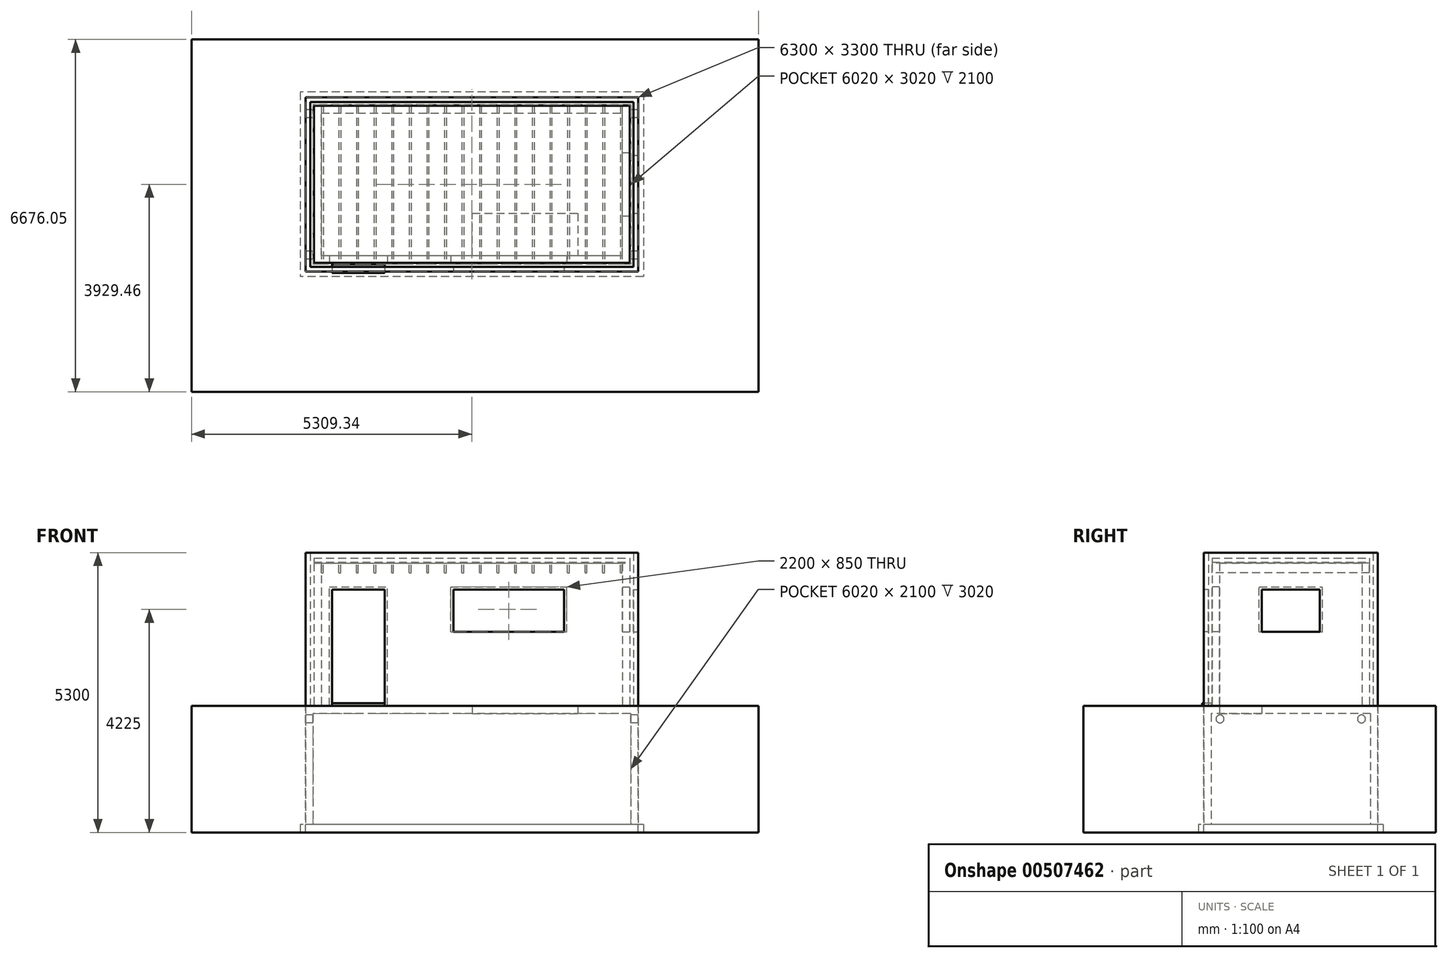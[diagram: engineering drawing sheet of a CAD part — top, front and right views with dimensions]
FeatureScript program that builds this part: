
annotation { "Feature Type Name" : "Feature", "Feature Type Description" : "" }
export const myFeature = defineFeature(function(context is Context, id is Id, definition is map)
    precondition{}
    {
        {
            var Q0;
            Q0=qCreatedBy(makeId("Top.planeOp"),FACE);
            var sketch = newSketch(context, id + "F0", { "sketchPlane" : qUnion([Q0])});
            skLineSegment(sketch, "E0.bottom", {"start": v(3250, 1750) * mm, "end": v(-3250, 1750) * mm});
            skLineSegment(sketch, "E0.top", {"start": v(3250, -1750) * mm, "end": v(-3250, -1750) * mm});
            skLineSegment(sketch, "E0.left", {"start": v(3250, 1750) * mm, "end": v(3250, -1750) * mm});
            skLineSegment(sketch, "E0.right", {"start": v(-3250, 1750) * mm, "end": v(-3250, -1750) * mm});
            skPoint(sketch, "E0.middle", {"position": v(0, 0) * mm});
            skSolve(sketch);
        }
        {
            var Q0;
            Q0=qSketchRegion(id+"F0",true);
            extrude(context, id + "F1", {"entities" : qUnion([Q0]), "depth" : 150 * mm});
        }
        {
            var Q0;
            Q0=makeQuery(id+"F1.opExtrude","CAP_FACE",FACE,{"disambiguationData":[OSD([sQuery(id+"F0.wireOp",EDGE,"E0.bottom"),sQuery(id+"F0.wireOp",EDGE,"E0.top"),sQuery(id+"F0.wireOp",EDGE,"E0.left"),sQuery(id+"F0.wireOp",EDGE,"E0.right")])],"isStart":false});
            var sketch = newSketch(context, id + "F2", { "sketchPlane" : qUnion([Q0])});
            skLineSegment(sketch, "E1.bottom", {"start": v(3010, 1510) * mm, "end": v(-3010, 1510) * mm});
            skLineSegment(sketch, "E1.top", {"start": v(3010, -1510) * mm, "end": v(-3010, -1510) * mm});
            skLineSegment(sketch, "E1.left", {"start": v(3010, 1510) * mm, "end": v(3010, -1510) * mm});
            skLineSegment(sketch, "E1.right", {"start": v(-3010, 1510) * mm, "end": v(-3010, -1510) * mm});
            skPoint(sketch, "E1.middle", {"position": v(0, 0) * mm});
            skLineSegment(sketch, "E2.bottom", {"start": v(3150, 1650) * mm, "end": v(-3150, 1650) * mm});
            skLineSegment(sketch, "E2.top", {"start": v(3150, -1650) * mm, "end": v(-3150, -1650) * mm});
            skLineSegment(sketch, "E2.left", {"start": v(3150, 1650) * mm, "end": v(3150, -1650) * mm});
            skLineSegment(sketch, "E2.right", {"start": v(-3150, 1650) * mm, "end": v(-3150, -1650) * mm});
            skSolve(sketch);
        }
        {
            var Q0;
            Q0=qSketchRegion(id+"F2",true);
            extrude(context, id + "F3", {"entities" : qUnion([Q0]), "operationType" : NewBodyOperationType.ADD, "depth" : 2100 * mm});
        }
        {
            var Q0;
            Q0=makeQuery(id+"F3.opExtrude","CAP_FACE",FACE,{"disambiguationData":[OSD([sQuery(id+"F2.wireOp",EDGE,"E1.bottom"),sQuery(id+"F2.wireOp",EDGE,"E1.top"),sQuery(id+"F2.wireOp",EDGE,"E1.left"),sQuery(id+"F2.wireOp",EDGE,"E1.right"),sQuery(id+"F2.wireOp",EDGE,"E2.bottom"),sQuery(id+"F2.wireOp",EDGE,"E2.top"),sQuery(id+"F2.wireOp",EDGE,"E2.left"),sQuery(id+"F2.wireOp",EDGE,"E2.right")])],"isStart":false});
            var sketch = newSketch(context, id + "F4", { "sketchPlane" : qUnion([Q0])});
            skLineSegment(sketch, "E3", {"start": v(10, -1350) * mm, "end": v(10, -550) * mm});
            skLineSegment(sketch, "E4", {"start": v(10, -550) * mm, "end": v(2010, -550) * mm});
            skLineSegment(sketch, "E5", {"start": v(3150, -1650) * mm, "end": v(3150, 1650) * mm});
            skLineSegment(sketch, "E6", {"start": v(3150, 1650) * mm, "end": v(-3150, 1650) * mm});
            skLineSegment(sketch, "E7", {"start": v(-3150, 1650) * mm, "end": v(-3150, -1650) * mm});
            skLineSegment(sketch, "E8", {"start": v(-3150, -1650) * mm, "end": v(3150, -1650) * mm});
            skLineSegment(sketch, "E9", {"start": v(2010, -550) * mm, "end": v(2010, -1350) * mm});
            skLineSegment(sketch, "E10", {"start": v(10, -1350) * mm, "end": v(2010, -1350) * mm});
            skSolve(sketch);
        }
        {
            var Q0;
            Q0=qSketchRegion(id+"F4",true);
            extrude(context, id + "F5", {"entities" : qUnion([Q0]), "operationType" : NewBodyOperationType.ADD, "depth" : 150 * mm});
        }
        {
            var Q0;
            Q0=makeQuery(id+"F5.boolean.opBoolean","MERGE",FACE,{"derivedFrom":[makeQuery(id+"F3.opExtrude","SWEPT_FACE",FACE,{"disambiguationData":[OSD([sQuery(id+"F2.wireOp",EDGE,"E2.right")])]}),makeQuery(id+"F5.opExtrude","SWEPT_FACE",FACE,{"disambiguationData":[OSD([sQuery(id+"F4.wireOp",EDGE,"E7")])]})]});
            var sketch = newSketch(context, id + "F6", { "sketchPlane" : qUnion([Q0])});
            skCircle(sketch, "E11", {"center": v(-1340, 2150) * mm, "radius": 75 * mm});
            skCircle(sketch, "E12", {"center": v(1340, 2150) * mm, "radius": 75 * mm});
            skSolve(sketch);
        }
        {
            var Q0;
            Q0=qSketchRegion(id+"F6",true);
            extrude(context, id + "F7", {"entities" : qUnion([Q0]), "operationType" : NewBodyOperationType.REMOVE, "endBound" : BoundingType.THROUGH_ALL, "oppositeDirection" : true, "depth" : 25 * mm});
        }
        {
            var Q0;
            Q0=makeQuery(id+"F5.opExtrude","CAP_FACE",FACE,{"disambiguationData":[OSD([sQuery(id+"F4.wireOp",EDGE,"E3"),sQuery(id+"F4.wireOp",EDGE,"E4"),sQuery(id+"F4.wireOp",EDGE,"E5"),sQuery(id+"F4.wireOp",EDGE,"E6"),sQuery(id+"F4.wireOp",EDGE,"E7"),sQuery(id+"F4.wireOp",EDGE,"E8"),sQuery(id+"F4.wireOp",EDGE,"E9"),sQuery(id+"F4.wireOp",EDGE,"E10")])],"isStart":false});
            var sketch = newSketch(context, id + "F8", { "sketchPlane" : qUnion([Q0])});
            skLineSegment(sketch, "E13.bottom", {"start": v(-3150, -1650) * mm, "end": v(3150, -1650) * mm});
            skLineSegment(sketch, "E13.top", {"start": v(-3150, 1650) * mm, "end": v(3150, 1650) * mm});
            skLineSegment(sketch, "E13.left", {"start": v(-3150, -1650) * mm, "end": v(-3150, 1650) * mm});
            skLineSegment(sketch, "E13.right", {"start": v(3150, -1650) * mm, "end": v(3150, 1650) * mm});
            skLineSegment(sketch, "E14.bottom", {"start": v(-3060, -1560) * mm, "end": v(3060, -1560) * mm});
            skLineSegment(sketch, "E14.top", {"start": v(-3060, 1560) * mm, "end": v(3060, 1560) * mm});
            skLineSegment(sketch, "E14.left", {"start": v(-3060, -1560) * mm, "end": v(-3060, 1560) * mm});
            skLineSegment(sketch, "E14.right", {"start": v(3060, -1560) * mm, "end": v(3060, 1560) * mm});
            skSolve(sketch);
        }
        {
            var Q0;
            Q0 = qSketchRegion(id + "F8", true);
            extrude(context, id + "F9", {"entities" : qUnion([Q0]), "depth" : 2900 * mm});
        }
        {
            var Q0;
            Q0=makeQuery(id+"F5.opExtrude","CAP_FACE",FACE,{"disambiguationData":[OSD([sQuery(id+"F4.wireOp",EDGE,"E3"),sQuery(id+"F4.wireOp",EDGE,"E4"),sQuery(id+"F4.wireOp",EDGE,"E5"),sQuery(id+"F4.wireOp",EDGE,"E6"),sQuery(id+"F4.wireOp",EDGE,"E7"),sQuery(id+"F4.wireOp",EDGE,"E8"),sQuery(id+"F4.wireOp",EDGE,"E9"),sQuery(id+"F4.wireOp",EDGE,"E10")])],"isStart":false});
            var sketch = newSketch(context, id + "F10", { "sketchPlane" : qUnion([Q0])});
            skLineSegment(sketch, "E15.bottom", {"start": v(-2990, -1490) * mm, "end": v(2990, -1490) * mm});
            skLineSegment(sketch, "E15.top", {"start": v(-2990, 1490) * mm, "end": v(2990, 1490) * mm});
            skLineSegment(sketch, "E15.left", {"start": v(-2990, -1490) * mm, "end": v(-2990, 1490) * mm});
            skLineSegment(sketch, "E15.right", {"start": v(2990, -1490) * mm, "end": v(2990, 1490) * mm});
            skLineSegment(sketch, "E16.bottom", {"start": v(-2850, -1350) * mm, "end": v(2850, -1350) * mm});
            skLineSegment(sketch, "E16.top", {"start": v(-2850, 1350) * mm, "end": v(2850, 1350) * mm});
            skLineSegment(sketch, "E16.left", {"start": v(-2850, -1350) * mm, "end": v(-2850, 1350) * mm});
            skLineSegment(sketch, "E16.right", {"start": v(2850, -1350) * mm, "end": v(2850, 1350) * mm});
            skSolve(sketch);
        }
        {
            var Q0;
            Q0 = qSketchRegion(id + "F10", true);
            extrude(context, id + "F11", {"entities" : qUnion([Q0]), "depth" : 2700 * mm});
        }
        {
            var Q0;
            Q0=makeQuery(id+"F9.opExtrude","SWEPT_FACE",FACE,{"disambiguationData":[OSD([sQuery(id+"F8.wireOp",EDGE,"E13.bottom")])]});
            var sketch = newSketch(context, id + "F12", { "sketchPlane" : qUnion([Q0])});
            skLineSegment(sketch, "E17.bottom", {"start": v(-2650, 2400) * mm, "end": v(-1650, 2400) * mm});
            skLineSegment(sketch, "E17.top", {"start": v(-2650, 4600) * mm, "end": v(-1650, 4600) * mm});
            skLineSegment(sketch, "E17.left", {"start": v(-2650, 2400) * mm, "end": v(-2650, 4600) * mm});
            skLineSegment(sketch, "E17.right", {"start": v(-1650, 2400) * mm, "end": v(-1650, 4600) * mm});
            skLineSegment(sketch, "E18.bottom", {"start": v(-350, 3800) * mm, "end": v(1750, 3800) * mm});
            skLineSegment(sketch, "E18.top", {"start": v(-350, 4600) * mm, "end": v(1750, 4600) * mm});
            skLineSegment(sketch, "E18.left", {"start": v(-350, 3800) * mm, "end": v(-350, 4600) * mm});
            skLineSegment(sketch, "E18.right", {"start": v(1750, 3800) * mm, "end": v(1750, 4600) * mm});
            skSolve(sketch);
        }
        {
            var Q0;
            Q0 = qSketchRegion(id + "F12", true);
            extrude(context, id + "F13", {"entities" : qUnion([Q0]), "operationType" : NewBodyOperationType.REMOVE, "endBound" : BoundingType.UP_TO_NEXT, "oppositeDirection" : true, "depth" : 25 * mm});
        }
        {
            var Q0;
            Q0=makeQuery(id+"F11.opExtrude","SWEPT_FACE",FACE,{"disambiguationData":[OSD([sQuery(id+"F10.wireOp",EDGE,"E15.bottom")])]});
            var sketch = newSketch(context, id + "F14", { "sketchPlane" : qUnion([Q0])});
            skLineSegment(sketch, "E19.bottom", {"start": v(-2700, 2400) * mm, "end": v(-1600, 2400) * mm});
            skLineSegment(sketch, "E19.top", {"start": v(-2700, 4650) * mm, "end": v(-1600, 4650) * mm});
            skLineSegment(sketch, "E19.left", {"start": v(-2700, 2400) * mm, "end": v(-2700, 4650) * mm});
            skLineSegment(sketch, "E19.right", {"start": v(-1600, 2400) * mm, "end": v(-1600, 4650) * mm});
            skLineSegment(sketch, "E20.bottom", {"start": v(-400, 3800) * mm, "end": v(1800, 3800) * mm});
            skLineSegment(sketch, "E20.top", {"start": v(-400, 4650) * mm, "end": v(1800, 4650) * mm});
            skLineSegment(sketch, "E20.left", {"start": v(-400, 3800) * mm, "end": v(-400, 4650) * mm});
            skLineSegment(sketch, "E20.right", {"start": v(1800, 3800) * mm, "end": v(1800, 4650) * mm});
            skSolve(sketch);
        }
        {
            var Q0;
            Q0 = qSketchRegion(id + "F14", true);
            extrude(context, id + "F15", {"entities" : qUnion([Q0]), "operationType" : NewBodyOperationType.REMOVE, "endBound" : BoundingType.UP_TO_NEXT, "oppositeDirection" : true, "depth" : 25 * mm});
        }
        {
            var Q0;
            Q0=makeQuery(id+"F9.opExtrude","SWEPT_FACE",FACE,{"disambiguationData":[OSD([sQuery(id+"F8.wireOp",EDGE,"E13.right")])]});
            var sketch = newSketch(context, id + "F16", { "sketchPlane" : qUnion([Q0])});
            skLineSegment(sketch, "E21.bottom", {"start": v(-550, 3800) * mm, "end": v(550, 3800) * mm});
            skLineSegment(sketch, "E21.top", {"start": v(-550, 4600) * mm, "end": v(550, 4600) * mm});
            skLineSegment(sketch, "E21.left", {"start": v(-550, 3800) * mm, "end": v(-550, 4600) * mm});
            skLineSegment(sketch, "E21.right", {"start": v(550, 3800) * mm, "end": v(550, 4600) * mm});
            skSolve(sketch);
        }
        {
            var Q0;
            Q0 = qSketchRegion(id + "F16", true);
            extrude(context, id + "F17", {"entities" : qUnion([Q0]), "operationType" : NewBodyOperationType.REMOVE, "endBound" : BoundingType.UP_TO_NEXT, "oppositeDirection" : true, "depth" : 25 * mm});
        }
        {
            var Q0;
            Q0=makeQuery(id+"F11.opExtrude","SWEPT_FACE",FACE,{"disambiguationData":[OSD([sQuery(id+"F10.wireOp",EDGE,"E15.right")])]});
            var sketch = newSketch(context, id + "F18", { "sketchPlane" : qUnion([Q0])});
            skLineSegment(sketch, "E22.bottom", {"start": v(-600, 3800) * mm, "end": v(600, 3800) * mm});
            skLineSegment(sketch, "E22.top", {"start": v(-600, 4650) * mm, "end": v(600, 4650) * mm});
            skLineSegment(sketch, "E22.left", {"start": v(-600, 3800) * mm, "end": v(-600, 4650) * mm});
            skLineSegment(sketch, "E22.right", {"start": v(600, 3800) * mm, "end": v(600, 4650) * mm});
            skSolve(sketch);
        }
        {
            var Q0;
            Q0 = qSketchRegion(id + "F18", true);
            extrude(context, id + "F19", {"entities" : qUnion([Q0]), "operationType" : NewBodyOperationType.REMOVE, "endBound" : BoundingType.UP_TO_NEXT, "oppositeDirection" : true, "depth" : 25 * mm});
        }
        {
            var Q0;
            Q0=makeQuery(id+"F11.opExtrude","CAP_FACE",FACE,{"disambiguationData":[OSD([sQuery(id+"F10.wireOp",EDGE,"E15.bottom"),sQuery(id+"F10.wireOp",EDGE,"E15.top"),sQuery(id+"F10.wireOp",EDGE,"E15.left"),sQuery(id+"F10.wireOp",EDGE,"E15.right"),sQuery(id+"F10.wireOp",EDGE,"E16.bottom"),sQuery(id+"F10.wireOp",EDGE,"E16.top"),sQuery(id+"F10.wireOp",EDGE,"E16.left"),sQuery(id+"F10.wireOp",EDGE,"E16.right")])],"isStart":false});
            var sketch = newSketch(context, id + "F20", { "sketchPlane" : qUnion([Q0])});
            skLineSegment(sketch, "E23.bottom", {"start": v(-2850, 1490) * mm, "end": v(-2815, 1490) * mm});
            skLineSegment(sketch, "E23.top", {"start": v(-2850, -1490) * mm, "end": v(-2815, -1490) * mm});
            skLineSegment(sketch, "E23.left", {"start": v(-2850, 1490) * mm, "end": v(-2850, -1490) * mm});
            skLineSegment(sketch, "E23.right", {"start": v(-2815, 1490) * mm, "end": v(-2815, -1490) * mm});
            skLineSegment(sketch, "E24.1.0.0", {"start": v(-2482, 1490) * mm, "end": v(-2482, -1490) * mm});
            skLineSegment(sketch, "E24.1.0.1", {"start": v(-2517, 1490) * mm, "end": v(-2482, 1490) * mm});
            skLineSegment(sketch, "E24.1.0.2", {"start": v(-2517, 1490) * mm, "end": v(-2517, -1490) * mm});
            skLineSegment(sketch, "E24.1.0.3", {"start": v(-2517, -1490) * mm, "end": v(-2482, -1490) * mm});
            skLineSegment(sketch, "E24.2.0.0", {"start": v(-2149, 1490) * mm, "end": v(-2149, -1490) * mm});
            skLineSegment(sketch, "E24.2.0.1", {"start": v(-2184, 1490) * mm, "end": v(-2149, 1490) * mm});
            skLineSegment(sketch, "E24.2.0.2", {"start": v(-2184, 1490) * mm, "end": v(-2184, -1490) * mm});
            skLineSegment(sketch, "E24.2.0.3", {"start": v(-2184, -1490) * mm, "end": v(-2149, -1490) * mm});
            skLineSegment(sketch, "E24.3.0.0", {"start": v(-1816, 1490) * mm, "end": v(-1816, -1490) * mm});
            skLineSegment(sketch, "E24.3.0.1", {"start": v(-1851, 1490) * mm, "end": v(-1816, 1490) * mm});
            skLineSegment(sketch, "E24.3.0.2", {"start": v(-1851, 1490) * mm, "end": v(-1851, -1490) * mm});
            skLineSegment(sketch, "E24.3.0.3", {"start": v(-1851, -1490) * mm, "end": v(-1816, -1490) * mm});
            skLineSegment(sketch, "E24.4.0.0", {"start": v(-1483, 1490) * mm, "end": v(-1483, -1490) * mm});
            skLineSegment(sketch, "E24.4.0.1", {"start": v(-1518, 1490) * mm, "end": v(-1483, 1490) * mm});
            skLineSegment(sketch, "E24.4.0.2", {"start": v(-1518, 1490) * mm, "end": v(-1518, -1490) * mm});
            skLineSegment(sketch, "E24.4.0.3", {"start": v(-1518, -1490) * mm, "end": v(-1483, -1490) * mm});
            skLineSegment(sketch, "E24.5.0.0", {"start": v(-1150, 1490) * mm, "end": v(-1150, -1490) * mm});
            skLineSegment(sketch, "E24.5.0.1", {"start": v(-1185, 1490) * mm, "end": v(-1150, 1490) * mm});
            skLineSegment(sketch, "E24.5.0.2", {"start": v(-1185, 1490) * mm, "end": v(-1185, -1490) * mm});
            skLineSegment(sketch, "E24.5.0.3", {"start": v(-1185, -1490) * mm, "end": v(-1150, -1490) * mm});
            skLineSegment(sketch, "E24.6.0.0", {"start": v(-817, 1490) * mm, "end": v(-817, -1490) * mm});
            skLineSegment(sketch, "E24.6.0.1", {"start": v(-852, 1490) * mm, "end": v(-817, 1490) * mm});
            skLineSegment(sketch, "E24.6.0.2", {"start": v(-852, 1490) * mm, "end": v(-852, -1490) * mm});
            skLineSegment(sketch, "E24.6.0.3", {"start": v(-852, -1490) * mm, "end": v(-817, -1490) * mm});
            skLineSegment(sketch, "E24.7.0.0", {"start": v(-484, 1490) * mm, "end": v(-484, -1490) * mm});
            skLineSegment(sketch, "E24.7.0.1", {"start": v(-519, 1490) * mm, "end": v(-484, 1490) * mm});
            skLineSegment(sketch, "E24.7.0.2", {"start": v(-519, 1490) * mm, "end": v(-519, -1490) * mm});
            skLineSegment(sketch, "E24.7.0.3", {"start": v(-519, -1490) * mm, "end": v(-484, -1490) * mm});
            skLineSegment(sketch, "E24.8.0.0", {"start": v(-151, 1490) * mm, "end": v(-151, -1490) * mm});
            skLineSegment(sketch, "E24.8.0.1", {"start": v(-186, 1490) * mm, "end": v(-151, 1490) * mm});
            skLineSegment(sketch, "E24.8.0.2", {"start": v(-186, 1490) * mm, "end": v(-186, -1490) * mm});
            skLineSegment(sketch, "E24.8.0.3", {"start": v(-186, -1490) * mm, "end": v(-151, -1490) * mm});
            skLineSegment(sketch, "E24.9.0.0", {"start": v(182, 1490) * mm, "end": v(182, -1490) * mm});
            skLineSegment(sketch, "E24.9.0.1", {"start": v(147, 1490) * mm, "end": v(182, 1490) * mm});
            skLineSegment(sketch, "E24.9.0.2", {"start": v(147, 1490) * mm, "end": v(147, -1490) * mm});
            skLineSegment(sketch, "E24.9.0.3", {"start": v(147, -1490) * mm, "end": v(182, -1490) * mm});
            skLineSegment(sketch, "E24.10.0.0", {"start": v(515, 1490) * mm, "end": v(515, -1490) * mm});
            skLineSegment(sketch, "E24.10.0.1", {"start": v(480, 1490) * mm, "end": v(515, 1490) * mm});
            skLineSegment(sketch, "E24.10.0.2", {"start": v(480, 1490) * mm, "end": v(480, -1490) * mm});
            skLineSegment(sketch, "E24.10.0.3", {"start": v(480, -1490) * mm, "end": v(515, -1490) * mm});
            skLineSegment(sketch, "E24.11.0.0", {"start": v(848, 1490) * mm, "end": v(848, -1490) * mm});
            skLineSegment(sketch, "E24.11.0.1", {"start": v(813, 1490) * mm, "end": v(848, 1490) * mm});
            skLineSegment(sketch, "E24.11.0.2", {"start": v(813, 1490) * mm, "end": v(813, -1490) * mm});
            skLineSegment(sketch, "E24.11.0.3", {"start": v(813, -1490) * mm, "end": v(848, -1490) * mm});
            skLineSegment(sketch, "E24.12.0.0", {"start": v(1181, 1490) * mm, "end": v(1181, -1490) * mm});
            skLineSegment(sketch, "E24.12.0.1", {"start": v(1146, 1490) * mm, "end": v(1181, 1490) * mm});
            skLineSegment(sketch, "E24.12.0.2", {"start": v(1146, 1490) * mm, "end": v(1146, -1490) * mm});
            skLineSegment(sketch, "E24.12.0.3", {"start": v(1146, -1490) * mm, "end": v(1181, -1490) * mm});
            skLineSegment(sketch, "E24.direction1", {"start": v(-2815, -1490) * mm, "end": v(-2482, -1490) * mm, "construction": true});
            skLineSegment(sketch, "E25.0.13.0", {"start": v(1514, 1490) * mm, "end": v(1514, -1490) * mm});
            skLineSegment(sketch, "E25.3.13.0", {"start": v(1479, 1490) * mm, "end": v(1514, 1490) * mm});
            skLineSegment(sketch, "E25.6.13.0", {"start": v(1479, 1490) * mm, "end": v(1479, -1490) * mm});
            skLineSegment(sketch, "E25.9.13.0", {"start": v(1479, -1490) * mm, "end": v(1514, -1490) * mm});
            skLineSegment(sketch, "E25.0.14.0", {"start": v(1847, 1490) * mm, "end": v(1847, -1490) * mm});
            skLineSegment(sketch, "E25.3.14.0", {"start": v(1812, 1490) * mm, "end": v(1847, 1490) * mm});
            skLineSegment(sketch, "E25.6.14.0", {"start": v(1812, 1490) * mm, "end": v(1812, -1490) * mm});
            skLineSegment(sketch, "E25.9.14.0", {"start": v(1812, -1490) * mm, "end": v(1847, -1490) * mm});
            skLineSegment(sketch, "E25.0.15.0", {"start": v(2180, 1490) * mm, "end": v(2180, -1490) * mm});
            skLineSegment(sketch, "E25.3.15.0", {"start": v(2145, 1490) * mm, "end": v(2180, 1490) * mm});
            skLineSegment(sketch, "E25.6.15.0", {"start": v(2145, 1490) * mm, "end": v(2145, -1490) * mm});
            skLineSegment(sketch, "E25.9.15.0", {"start": v(2145, -1490) * mm, "end": v(2180, -1490) * mm});
            skLineSegment(sketch, "E25.0.16.0", {"start": v(2513, 1490) * mm, "end": v(2513, -1490) * mm});
            skLineSegment(sketch, "E25.3.16.0", {"start": v(2478, 1490) * mm, "end": v(2513, 1490) * mm});
            skLineSegment(sketch, "E25.6.16.0", {"start": v(2478, 1490) * mm, "end": v(2478, -1490) * mm});
            skLineSegment(sketch, "E25.9.16.0", {"start": v(2478, -1490) * mm, "end": v(2513, -1490) * mm});
            skLineSegment(sketch, "E26.0.17.0", {"start": v(2846, 1490) * mm, "end": v(2846, -1490) * mm});
            skLineSegment(sketch, "E26.3.17.0", {"start": v(2811, 1490) * mm, "end": v(2846, 1490) * mm});
            skLineSegment(sketch, "E26.6.17.0", {"start": v(2811, 1490) * mm, "end": v(2811, -1490) * mm});
            skLineSegment(sketch, "E26.9.17.0", {"start": v(2811, -1490) * mm, "end": v(2846, -1490) * mm});
            skSolve(sketch);
        }
        {
            var Q0;
            Q0 = qSketchRegion(id + "F20", true);
            extrude(context, id + "F21", {"entities" : qUnion([Q0]), "oppositeDirection" : true, "depth" : 180 * mm});
        }
        {
            var Q0;
            Q0=makeQuery(id+"F11.opExtrude","CAP_FACE",FACE,{"disambiguationData":[OSD([sQuery(id+"F10.wireOp",EDGE,"E15.bottom"),sQuery(id+"F10.wireOp",EDGE,"E15.top"),sQuery(id+"F10.wireOp",EDGE,"E15.left"),sQuery(id+"F10.wireOp",EDGE,"E15.right"),sQuery(id+"F10.wireOp",EDGE,"E16.bottom"),sQuery(id+"F10.wireOp",EDGE,"E16.top"),sQuery(id+"F10.wireOp",EDGE,"E16.left"),sQuery(id+"F10.wireOp",EDGE,"E16.right")])],"isStart":false});
            var sketch = newSketch(context, id + "F22", { "sketchPlane" : qUnion([Q0])});
            skLineSegment(sketch, "E27.bottom", {"start": v(-2990, 1490) * mm, "end": v(2990, 1490) * mm});
            skLineSegment(sketch, "E27.top", {"start": v(-2990, -1490) * mm, "end": v(2990, -1490) * mm});
            skLineSegment(sketch, "E27.left", {"start": v(-2990, 1490) * mm, "end": v(-2990, -1490) * mm});
            skLineSegment(sketch, "E27.right", {"start": v(2990, 1490) * mm, "end": v(2990, -1490) * mm});
            skSolve(sketch);
        }
        {
            var Q0;
            Q0 = qSketchRegion(id + "F22", true);
            extrude(context, id + "F23", {"entities" : qUnion([Q0]), "depth" : 20 * mm});
        }
        {
            var Q0;
            Q0=makeQuery(id+"F23.opExtrude","CAP_FACE",FACE,{"disambiguationData":[OSD([sQuery(id+"F22.wireOp",EDGE,"E27.bottom"),sQuery(id+"F22.wireOp",EDGE,"E27.top"),sQuery(id+"F22.wireOp",EDGE,"E27.left"),sQuery(id+"F22.wireOp",EDGE,"E27.right")])],"isStart":false});
            var sketch = newSketch(context, id + "F24", { "sketchPlane" : qUnion([Q0])});
            skLineSegment(sketch, "E28.bottom", {"start": v(-2990, 1490) * mm, "end": v(2990, 1490) * mm});
            skLineSegment(sketch, "E28.top", {"start": v(-2990, -1490) * mm, "end": v(2990, -1490) * mm});
            skLineSegment(sketch, "E28.left", {"start": v(-2990, 1490) * mm, "end": v(-2990, -1490) * mm});
            skLineSegment(sketch, "E28.right", {"start": v(2990, 1490) * mm, "end": v(2990, -1490) * mm});
            skSolve(sketch);
        }
        {
            var Q0;
            Q0 = qSketchRegion(id + "F24", true);
            extrude(context, id + "F25", {"entities" : qUnion([Q0]), "depth" : 80 * mm});
        }
        {
            var Q0;
            Q0=makeQuery(id+"F5.opExtrude","CAP_FACE",FACE,{"disambiguationData":[OSD([sQuery(id+"F4.wireOp",EDGE,"E3"),sQuery(id+"F4.wireOp",EDGE,"E4"),sQuery(id+"F4.wireOp",EDGE,"E5"),sQuery(id+"F4.wireOp",EDGE,"E6"),sQuery(id+"F4.wireOp",EDGE,"E7"),sQuery(id+"F4.wireOp",EDGE,"E8"),sQuery(id+"F4.wireOp",EDGE,"E9"),sQuery(id+"F4.wireOp",EDGE,"E10")])],"isStart":false});
            var sketch = newSketch(context, id + "F26", { "sketchPlane" : qUnion([Q0])});
            skLineSegment(sketch, "E29.bottom", {"start": v(-1650, -1510) * mm, "end": v(-2650, -1510) * mm});
            skLineSegment(sketch, "E29.top", {"start": v(-1650, -1680) * mm, "end": v(-2650, -1680) * mm});
            skLineSegment(sketch, "E29.left", {"start": v(-1650, -1510) * mm, "end": v(-1650, -1680) * mm});
            skLineSegment(sketch, "E29.right", {"start": v(-2650, -1510) * mm, "end": v(-2650, -1680) * mm});
            skSolve(sketch);
        }
        {
            var Q0;
            Q0 = qSketchRegion(id + "F26", true);
            extrude(context, id + "F27", {"entities" : qUnion([Q0]), "depth" : 50 * mm});
        }
        {
            var Q0;
            Q0=makeQuery(id+"F5.opExtrude","CAP_FACE",FACE,{"disambiguationData":[OSD([sQuery(id+"F4.wireOp",EDGE,"E3"),sQuery(id+"F4.wireOp",EDGE,"E4"),sQuery(id+"F4.wireOp",EDGE,"E5"),sQuery(id+"F4.wireOp",EDGE,"E6"),sQuery(id+"F4.wireOp",EDGE,"E7"),sQuery(id+"F4.wireOp",EDGE,"E8"),sQuery(id+"F4.wireOp",EDGE,"E9"),sQuery(id+"F4.wireOp",EDGE,"E10")])],"isStart":false});
            var sketch = newSketch(context, id + "F28", { "sketchPlane" : qUnion([Q0])});
            skLineSegment(sketch, "E30.bottom", {"start": v(-3150, -1650) * mm, "end": v(3150, -1650) * mm});
            skLineSegment(sketch, "E30.top", {"start": v(-3150, 1650) * mm, "end": v(3150, 1650) * mm});
            skLineSegment(sketch, "E30.left", {"start": v(-3150, -1650) * mm, "end": v(-3150, 1650) * mm});
            skLineSegment(sketch, "E30.right", {"start": v(3150, -1650) * mm, "end": v(3150, 1650) * mm});
            skLineSegment(sketch, "E31.bottom", {"start": v(-5309.34, -3929.46) * mm, "end": v(5428.75, -3929.46) * mm});
            skLineSegment(sketch, "E31.top", {"start": v(-5309.34, 2746.59) * mm, "end": v(5428.75, 2746.59) * mm});
            skLineSegment(sketch, "E31.left", {"start": v(-5309.34, -3929.46) * mm, "end": v(-5309.34, 2746.59) * mm});
            skLineSegment(sketch, "E31.right", {"start": v(5428.75, -3929.46) * mm, "end": v(5428.75, 2746.59) * mm});
            skSolve(sketch);
        }
        {
            var Q0;
            Q0 = qSketchRegion(id + "F28", true);
            extrude(context, id + "F29", {"entities" : qUnion([Q0]), "oppositeDirection" : true, "depth" : 2400 * mm});
        }
    });
